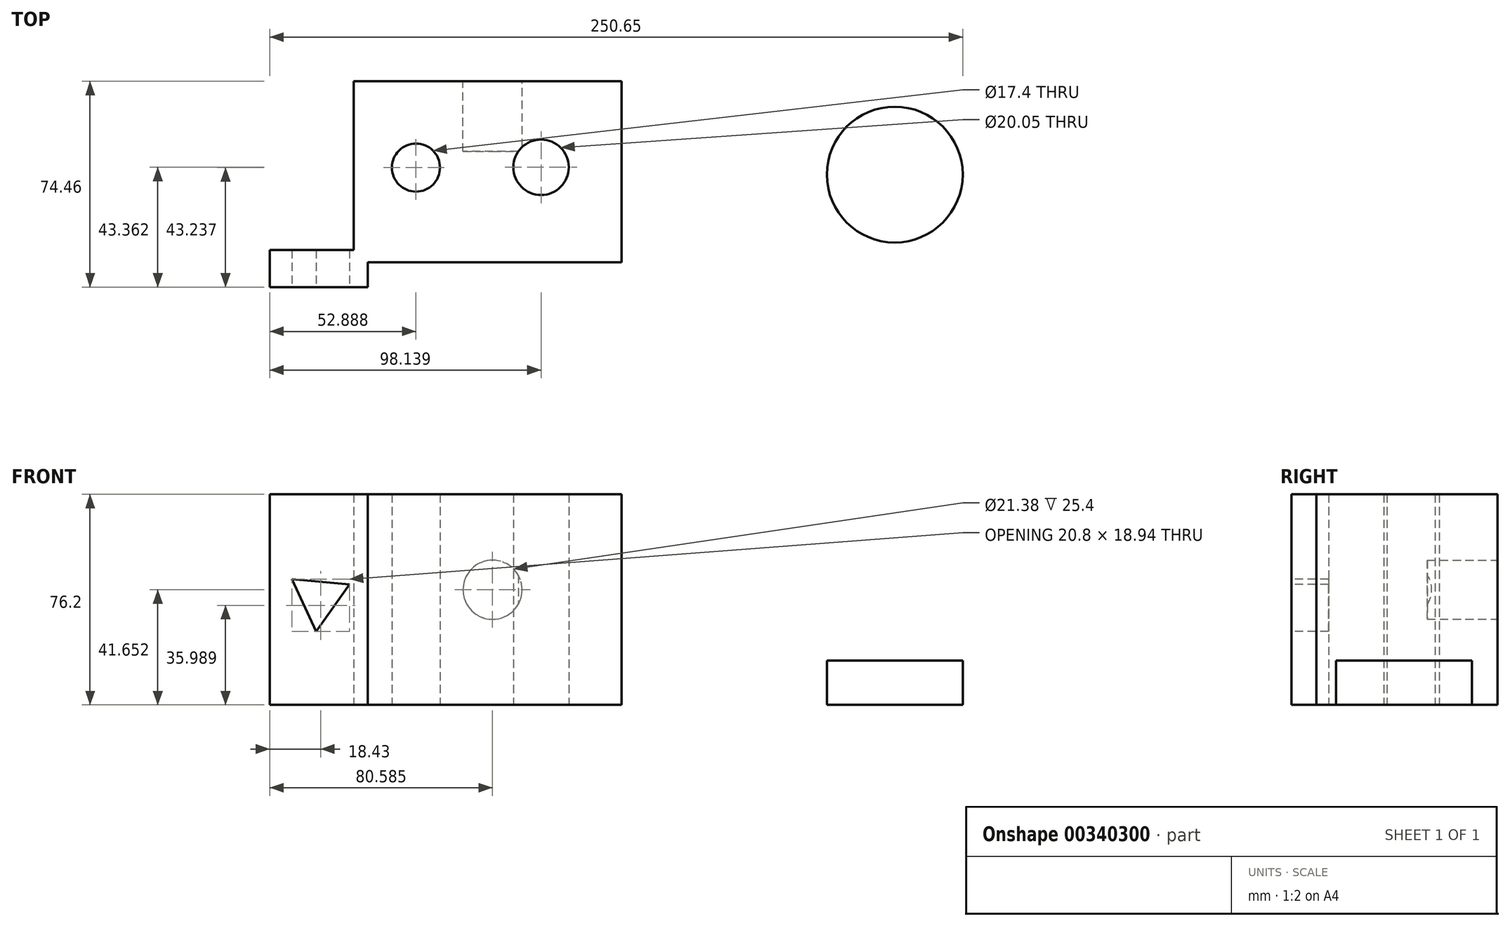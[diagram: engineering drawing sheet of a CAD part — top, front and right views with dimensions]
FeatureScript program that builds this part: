
annotation { "Feature Type Name" : "Feature", "Feature Type Description" : "" }
export const myFeature = defineFeature(function(context is Context, id is Id, definition is map)
    precondition{}
    {
        {
            var Q0;
            Q0=qCreatedBy(makeId("Top.planeOp"),FACE);
            var sketch = newSketch(context, id + "F0", { "sketchPlane" : qUnion([Q0])});
            skLineSegment(sketch, "E0.bottom", {"start": v(-71.63, 40.98) * mm, "end": v(25.34, 40.98) * mm});
            skLineSegment(sketch, "E0.top", {"start": v(-66.5, -24.52) * mm, "end": v(25.34, -24.52) * mm});
            skLineSegment(sketch, "E0.left", {"start": v(-71.63, 40.98) * mm, "end": v(-71.63, -20.08) * mm});
            skLineSegment(sketch, "E0.right", {"start": v(25.34, 40.98) * mm, "end": v(25.34, -24.52) * mm});
            skCircle(sketch, "E1", {"center": v(-49.05, 9.76) * mm, "radius": 8.7 * mm});
            skCircle(sketch, "E2", {"center": v(-3.8, 9.88) * mm, "radius": 10.03 * mm});
            skLineSegment(sketch, "E3.bottom", {"start": v(-71.63, -20.08) * mm, "end": v(-101.94, -20.08) * mm});
            skLineSegment(sketch, "E3.top", {"start": v(-66.5, -33.48) * mm, "end": v(-101.94, -33.48) * mm});
            skLineSegment(sketch, "E3.left", {"start": v(-66.5, -24.52) * mm, "end": v(-66.5, -33.48) * mm});
            skLineSegment(sketch, "E3.right", {"start": v(-101.94, -20.08) * mm, "end": v(-101.94, -33.48) * mm});
            skSolve(sketch);
        }
        {
            var Q0;
            Q0 = qSketchRegion(id + "F0", true);
            extrude(context, id + "F1", {"entities" : qUnion([Q0]), "depth" : 76.2 * mm});
        }
        {
            var Q0;
            Q0=makeQuery(id+"F1.opExtrude","SWEPT_FACE",FACE,{"disambiguationData":[OSD([sQuery(id+"F0.wireOp",EDGE,"E3.top")])]});
            var sketch = newSketch(context, id + "F2", { "sketchPlane" : qUnion([Q0])});
            skCircle(sketch, "E4.cCircle", {"center": v(-84.05, 38.53) * mm, "radius": 6.03 * mm, "construction": true});
            skLineSegment(sketch, "E4.0", {"start": v(-73.11, 43.6) * mm, "end": v(-85.12, 26.52) * mm});
            skLineSegment(sketch, "E4.1", {"start": v(-85.12, 26.52) * mm, "end": v(-93.9, 45.46) * mm});
            skLineSegment(sketch, "E4.2", {"start": v(-93.9, 45.46) * mm, "end": v(-73.11, 43.6) * mm});
            skPoint(sketch, "E4.0.midPoint", {"position": v(-79.11, 35.06) * mm});
            skSolve(sketch);
        }
        {
            var Q0;
            Q0 = qSketchRegion(id + "F2", true);
            extrude(context, id + "F3", {"entities" : qUnion([Q0]), "operationType" : NewBodyOperationType.REMOVE, "oppositeDirection" : true, "depth" : 49.53 * mm});
        }
        {
            var Q0;
            Q0=makeQuery(id+"F1.opExtrude","SWEPT_FACE",FACE,{"disambiguationData":[OSD([sQuery(id+"F0.wireOp",EDGE,"E0.bottom")])]});
            var sketch = newSketch(context, id + "F4", { "sketchPlane" : qUnion([Q0])});
            skCircle(sketch, "E5", {"center": v(21.36, 41.65) * mm, "radius": 10.7 * mm});
            skSolve(sketch);
        }
        {
            var Q0;
            Q0 = qSketchRegion(id + "F4", true);
            extrude(context, id + "F5", {"entities" : qUnion([Q0]), "operationType" : NewBodyOperationType.REMOVE, "oppositeDirection" : true, "depth" : 25.4 * mm});
        }
        {
            var Q0;
            Q0=qCreatedBy(makeId("Top.planeOp"),FACE);
            var sketch = newSketch(context, id + "F6", { "sketchPlane" : qUnion([Q0])});
            skCircle(sketch, "E6", {"center": v(124.14, 7.22) * mm, "radius": 24.57 * mm});
            skSolve(sketch);
        }
        {
            var Q0;
            Q0 = qSketchRegion(id + "F6", true);
            extrude(context, id + "F7", {"entities" : qUnion([Q0]), "depth" : 16 * mm});
        }
    });
